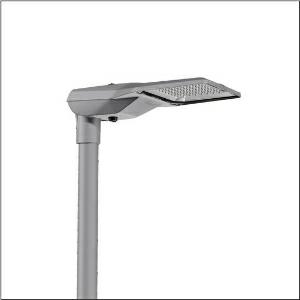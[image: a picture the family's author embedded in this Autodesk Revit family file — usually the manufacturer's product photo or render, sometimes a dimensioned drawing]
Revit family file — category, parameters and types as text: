
# Revit family: streetlight_sl_21_midi___st0_8a_5xe3c63t08nb_b211
name_source: partatom
category: Lighting Fixtures
units: mm (PartAtom-declared; Revit-internal decimal feet)

## family parameters
Cut with Voids When Loaded = No
Host = Face
Light Source = No
Part Type = Normal
Room Calculation Point = No
Round Connector Dimension = Use Diameter
Shared = No

## types (1)
- --- (1 x LED, 20350 lm, 151.2 W, 2700K)
    Apparent Load = 151 VA
    CIE Flux Codes = 41 75 97 100 100
    Color Rendering = 70
    Color Temperature = 2700K
    Default Elevation = 1800 mm
    Description = Streetlight SL 21 midi, mast luminaire, primary light control with lens, of PMMA, primary optical cover: cover, of toughened safety glass, transparent, light distribution: ST0.8a, light emission: direct distribution, primary light characteristic: asymmetric, installation type: side-entry, post-top, LED, High Power LED, rated luminous flux: 20.350lm, luminous efficacy: 135lm/W, light colour: 727, colour temperature: 2700K, control gear: D4i, control: overheat protection, constant luminous flux control, time-dependent luminous flux control, flexible luminous flux parameterisation, pre-setting: logarithmic dimming characteristic, mains connection: 230..240V, AC, 50/60Hz, start of lifetime: 151W, end of service life: 157W, reduction: 70W, luminaire housing, of diecast aluminium, powder-coated, Siteco® metallic grey (DB 702S), corrosivity category C5 mid according to DIN EN ISO 12944, please order mast flange separately, inclination adjustable: 0°, 5°, 10°, 15°, sealing non-destructively replaceable, multi-level sealing system, length: 644mm, width: 335mm, height: 110mm, mast flange for spigot size: 42mm (side-entry): 5XC10008XM4, 60/48mm (side-entry/post-top): 5XC10108XM2, 76/60mm (side-entry/post-top): 5XC10108XM1, mounting height: 4..8m, Smart Interface below and above, protection rating (complete): IP66, insulation class (complete): insulation class II (safety insulation), certification: CE, ENEC, ENEC+, VDE, impact resistance: IK10, permissible operating ambient temperature for outdoor applications: -40..+50°C, standard-compliant lighting for roads and squares, packaging unit: 1 piece

Light Distribution: ST0.8a
    Height = 111 mm
    Lamp = 1 x LED
    Lamp Light Flux = 20350 lm
    Lamp Power = 151.2 W
    Lamp count = 1
    Length = 644 mm
    Luminous efficacy = 135 lm/W
    Manufacturer = Siteco
    ModVariant = No
    Model = 5XE3C63T08NB
    Number of Poles = 1
    OnlyDefault = Yes
    Power Factor = 1
    Product Name = Streetlight SL 21 midi | ST0.8a
    Product group = mast luminaire | pylon top
    ProductGroupID = 6100
    Protection Class = Protection class II
    Protection Degree = IP 66
    RLX_Detail_Level = 1
    RLX_Emergency_Light_Flux = 0 lm
    RLX_Emergency_Type = 0
    RLX_Emergency_Type_DB = No
    RlxData = <blob elided: 27125 chars, md5=f5f5132f>
    Socket = socket
    Standby Power = 0 W
    System Light Flux = 20350 lm
    System Power = 151 W
    Type Comments = factory setting: luminous flux: 100 % | dim-lin: 254 | 802 mA
    Type Image = l_1004304.jpg
    URL = http://relux.com
    VarID = @adj_168568
    Voltage = 0 V
    Weight = 0.00 kg
    Width = 336 mm

## geometry (parser evidence)
native form markers: Blend x4, Sweep x13
no freeform markers — native parametric forms only
